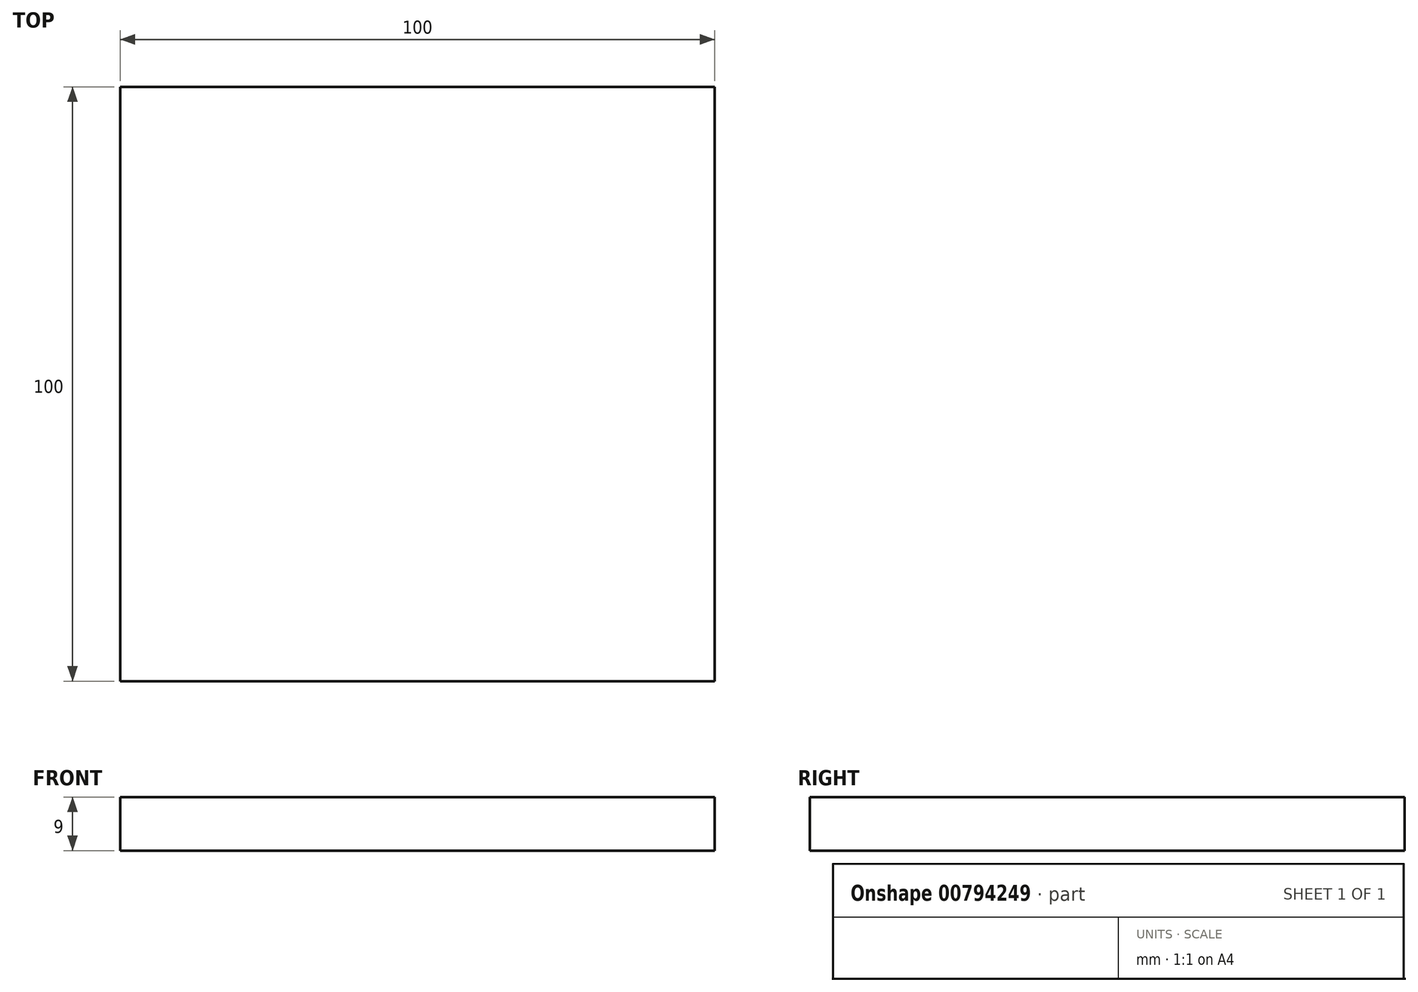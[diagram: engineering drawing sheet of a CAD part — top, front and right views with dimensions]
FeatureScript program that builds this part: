
annotation { "Feature Type Name" : "Feature", "Feature Type Description" : "" }
export const myFeature = defineFeature(function(context is Context, id is Id, definition is map)
    precondition{}
    {
        {
            var Q0;
            Q0=qCreatedBy(makeId("Top.planeOp"),FACE);
            var sketch = newSketch(context, id + "F0", { "sketchPlane" : qUnion([Q0])});
            skLineSegment(sketch, "E0.bottom", {"start": v(50, 50) * mm, "end": v(-50, 50) * mm});
            skLineSegment(sketch, "E0.top", {"start": v(50, -50) * mm, "end": v(-50, -50) * mm});
            skLineSegment(sketch, "E0.left", {"start": v(50, 50) * mm, "end": v(50, -50) * mm});
            skLineSegment(sketch, "E0.right", {"start": v(-50, 50) * mm, "end": v(-50, -50) * mm});
            skPoint(sketch, "E0.middle", {"position": v(0, 0) * mm});
            skSolve(sketch);
        }
        {
            var Q0;
            Q0=makeQuery(id+"F0.imprint","IMPRINT",FACE,{"disambiguationData":[TD([[makeQuery(id+"F0.imprint","IMPRINT",EDGE,{"derivedFrom":sQuery(id+"F0.wireOp",EDGE,"E0.bottom")}),1.0]])]});
            extrude(context, id + "F1", {"entities" : qUnion([Q0]), "depth" : 9 * mm, "offsetDistance" : 25 * mm});
        }
    });
